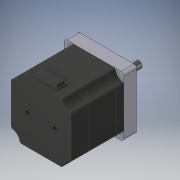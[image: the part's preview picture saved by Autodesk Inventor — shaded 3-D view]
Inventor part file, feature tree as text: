
AUTODESK INVENTOR PART (.ipt)
format: ipt  version: 2019 (Build 230136000, 136)  size: 240,128 bytes
history: native  units: in
note: dims shown in document units (in); Inventor stores cm internally (conversion verified against a paired STEP export)
features: other x4, chamfer x2
ambient origin geometry x8: Origin, YZ Plane, XZ Plane, XY Plane, X Axis, Y Axis, Z Axis, Center Point
bodies: Solid1 (feature_tree), Solid2 (feature_tree), Solid3 (feature_tree), Solid4 (feature_tree), Solid5 (feature_tree), Solid6 (feature_tree)
feature tree (6):
  other  "Boss-Extrude2"
  other  "Boss-Extrude3"
  chamfer  "Chamfer4"  [1 undecoded]
  other  "Cut-Extrude2"
  other  "Cut-Extrude3"
  chamfer  "Chamfer1"  [1 undecoded]
note: 2 required parameter values undecoded (feature->parameter linkage not recoverable at this tier; creation-order binding heuristic only, values carry confidence <= 0.55)
